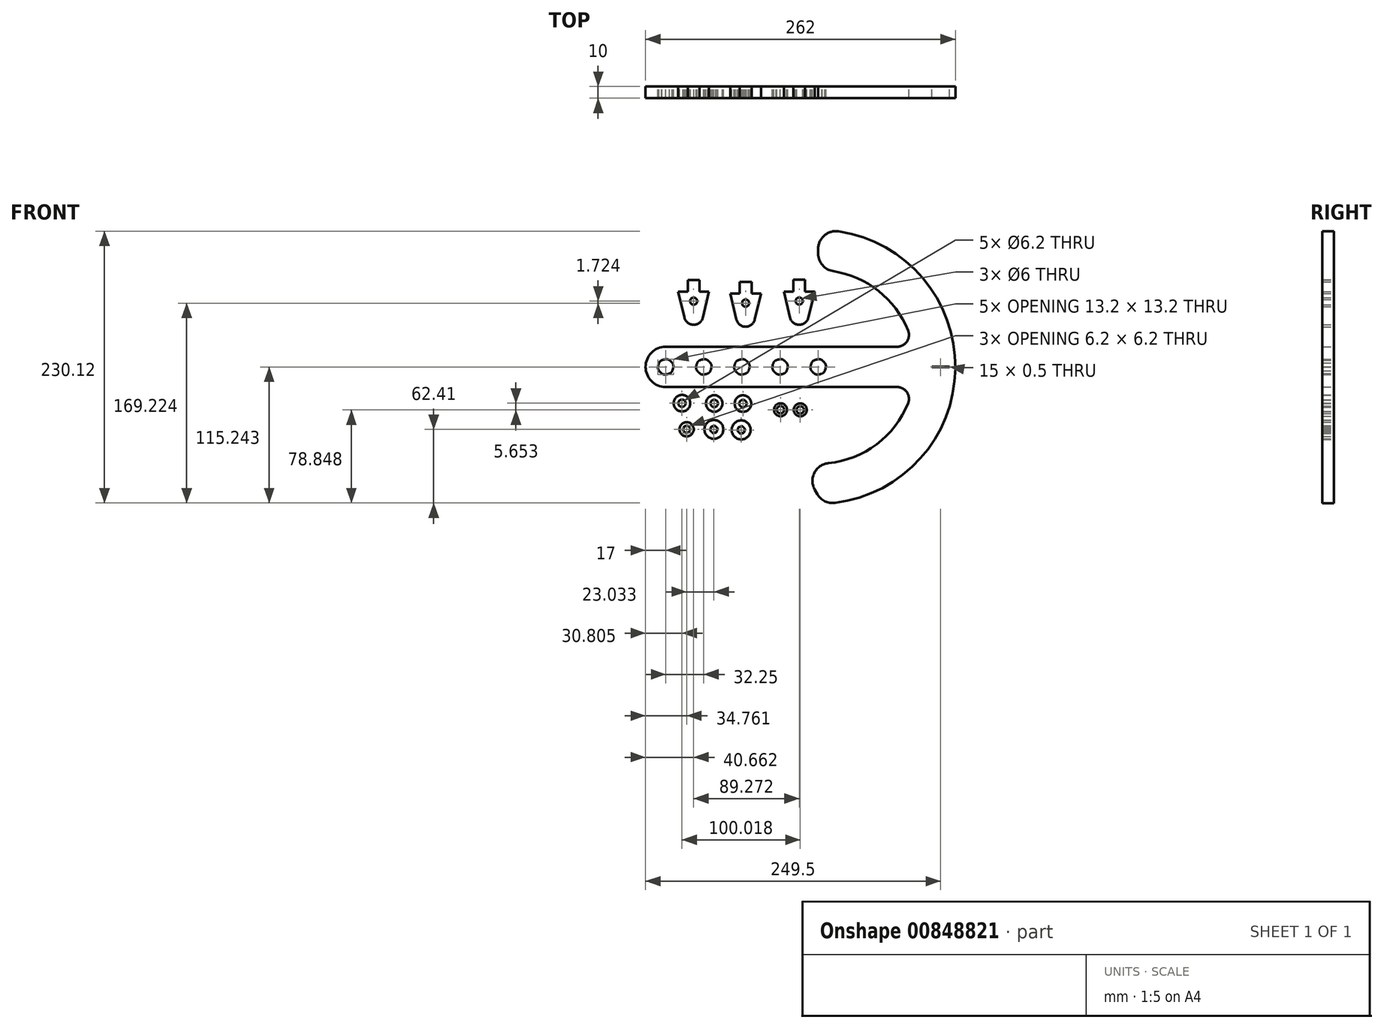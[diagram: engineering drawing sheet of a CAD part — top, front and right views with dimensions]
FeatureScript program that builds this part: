
annotation { "Feature Type Name" : "Feature", "Feature Type Description" : "" }
export const myFeature = defineFeature(function(context is Context, id is Id, definition is map)
    precondition{}
    {
        {
            var Q0;
            Q0=qCreatedBy(makeId("Front.planeOp"),FACE);
            var sketch = newSketch(context, id + "F0", { "sketchPlane" : qUnion([Q0])});
            skCircle(sketch, "E0", {"center": v(-90.34, 55.81) * mm, "radius": 3 * mm});
            skLineSegment(sketch, "E1", {"start": v(-103.34, 63.81) * mm, "end": v(-98.12, 41.96) * mm});
            skLineSegment(sketch, "E2", {"start": v(-77.34, 63.81) * mm, "end": v(-82.56, 41.96) * mm});
            skArc(sketch, "E3", {"start": v(-98.12, 41.96) * mm, "mid": v(-90.34, 35.81) * mm, "end": v(-82.56, 41.96) * mm});
            skLineSegment(sketch, "E4", {"start": v(-85.34, 63.81) * mm, "end": v(-77.34, 63.81) * mm});
            skLineSegment(sketch, "E5", {"start": v(-85.34, 73.81) * mm, "end": v(-85.34, 63.81) * mm});
            skLineSegment(sketch, "E6", {"start": v(-95.34, 73.81) * mm, "end": v(-85.34, 73.81) * mm});
            skLineSegment(sketch, "E7", {"start": v(-95.34, 63.81) * mm, "end": v(-95.34, 73.81) * mm});
            skLineSegment(sketch, "E8", {"start": v(-103.34, 63.81) * mm, "end": v(-95.34, 63.81) * mm});
            skCircle(sketch, "E9", {"center": v(-46.4, 54.16) * mm, "radius": 3 * mm});
            skLineSegment(sketch, "E10", {"start": v(-59.4, 62.16) * mm, "end": v(-54.17, 40.3) * mm});
            skLineSegment(sketch, "E11", {"start": v(-33.4, 62.16) * mm, "end": v(-38.6, 40.3) * mm});
            skArc(sketch, "E12", {"start": v(-54.17, 40.3) * mm, "mid": v(-46.4, 34.16) * mm, "end": v(-38.6, 40.3) * mm});
            skLineSegment(sketch, "E13", {"start": v(-41.4, 62.16) * mm, "end": v(-33.4, 62.16) * mm});
            skLineSegment(sketch, "E14", {"start": v(-41.4, 72.16) * mm, "end": v(-41.4, 62.16) * mm});
            skLineSegment(sketch, "E15", {"start": v(-51.4, 72.16) * mm, "end": v(-41.4, 72.16) * mm});
            skLineSegment(sketch, "E16", {"start": v(-51.4, 62.16) * mm, "end": v(-51.4, 72.16) * mm});
            skLineSegment(sketch, "E17", {"start": v(-59.4, 62.16) * mm, "end": v(-51.4, 62.16) * mm});
            skArc(sketch, "E18", {"start": v(18.3, 5.9) * mm, "mid": v(16.7, 6.56) * mm, "end": v(15, 6.78) * mm});
            skArc(sketch, "E19", {"start": v(21.6, 0.18) * mm, "mid": v(21.38, 1.9) * mm, "end": v(20.72, 3.48) * mm});
            skArc(sketch, "E20", {"start": v(18.3, -5.53) * mm, "mid": v(19.67, -4.48) * mm, "end": v(20.72, -3.12) * mm});
            skArc(sketch, "E21", {"start": v(11.7, -5.53) * mm, "mid": v(13.3, -6.2) * mm, "end": v(15, -6.42) * mm});
            skCircle(sketch, "E22", {"center": v(-1.07, 55.89) * mm, "radius": 3 * mm});
            skArc(sketch, "E23", {"start": v(8.4, 0.18) * mm, "mid": v(8.62, -1.53) * mm, "end": v(9.28, -3.12) * mm});
            skArc(sketch, "E24", {"start": v(20.54, 3.38) * mm, "mid": v(19.53, 4.7) * mm, "end": v(18.2, 5.73) * mm});
            skArc(sketch, "E25", {"start": v(20.54, -3.02) * mm, "mid": v(21.18, -1.47) * mm, "end": v(21.4, 0.18) * mm});
            skArc(sketch, "E26", {"start": v(15, -6.22) * mm, "mid": v(16.66, -6) * mm, "end": v(18.2, -5.36) * mm});
            skArc(sketch, "E27", {"start": v(9.46, -3.02) * mm, "mid": v(10.47, -4.34) * mm, "end": v(11.8, -5.36) * mm});
            skArc(sketch, "E28", {"start": v(9.46, 3.38) * mm, "mid": v(8.82, 1.84) * mm, "end": v(8.6, 0.18) * mm});
            skLineSegment(sketch, "E29", {"start": v(18.2, 5.73) * mm, "end": v(18.3, 5.9) * mm});
            skLineSegment(sketch, "E30", {"start": v(20.54, 3.38) * mm, "end": v(20.72, 3.48) * mm});
            skLineSegment(sketch, "E31", {"start": v(20.54, -3.02) * mm, "end": v(20.72, -3.12) * mm});
            skLineSegment(sketch, "E32", {"start": v(18.2, -5.36) * mm, "end": v(18.3, -5.53) * mm});
            skLineSegment(sketch, "E33", {"start": v(15, -6.22) * mm, "end": v(15, -6.42) * mm});
            skLineSegment(sketch, "E34", {"start": v(11.8, -5.36) * mm, "end": v(11.7, -5.53) * mm});
            skLineSegment(sketch, "E35", {"start": v(9.46, -3.02) * mm, "end": v(9.28, -3.12) * mm});
            skLineSegment(sketch, "E36", {"start": v(8.6, 0.18) * mm, "end": v(8.4, 0.18) * mm});
            skLineSegment(sketch, "E37", {"start": v(9.46, 3.38) * mm, "end": v(9.28, 3.48) * mm});
            skLineSegment(sketch, "E38", {"start": v(11.8, 5.73) * mm, "end": v(11.7, 5.9) * mm});
            skLineSegment(sketch, "E39", {"start": v(15, 6.58) * mm, "end": v(15, 6.78) * mm});
            skArc(sketch, "E40", {"start": v(15, 6.58) * mm, "mid": v(13.34, 6.37) * mm, "end": v(11.8, 5.73) * mm});
            skArc(sketch, "E41", {"start": v(11.7, 5.9) * mm, "mid": v(10.33, 4.85) * mm, "end": v(9.28, 3.48) * mm});
            skArc(sketch, "E42", {"start": v(-13.95, 5.9) * mm, "mid": v(-15.54, 6.56) * mm, "end": v(-17.25, 6.78) * mm});
            skArc(sketch, "E43", {"start": v(-10.65, 0.18) * mm, "mid": v(-10.87, 1.9) * mm, "end": v(-11.53, 3.48) * mm});
            skArc(sketch, "E44", {"start": v(-13.95, -5.53) * mm, "mid": v(-12.58, -4.48) * mm, "end": v(-11.53, -3.12) * mm});
            skArc(sketch, "E45", {"start": v(-20.55, -5.53) * mm, "mid": v(-18.96, -6.2) * mm, "end": v(-17.25, -6.42) * mm});
            skArc(sketch, "E46", {"start": v(-23.85, 0.18) * mm, "mid": v(-23.63, -1.53) * mm, "end": v(-22.97, -3.12) * mm});
            skArc(sketch, "E47", {"start": v(-11.7, 3.38) * mm, "mid": v(-12.72, 4.7) * mm, "end": v(-14.05, 5.73) * mm});
            skArc(sketch, "E48", {"start": v(-11.7, -3.02) * mm, "mid": v(-11.07, -1.47) * mm, "end": v(-10.85, 0.18) * mm});
            skArc(sketch, "E49", {"start": v(-17.25, -6.22) * mm, "mid": v(-15.6, -6) * mm, "end": v(-14.05, -5.36) * mm});
            skArc(sketch, "E50", {"start": v(-22.8, -3.02) * mm, "mid": v(-21.78, -4.34) * mm, "end": v(-20.45, -5.36) * mm});
            skArc(sketch, "E51", {"start": v(-22.8, 3.38) * mm, "mid": v(-23.43, 1.84) * mm, "end": v(-23.65, 0.18) * mm});
            skLineSegment(sketch, "E52", {"start": v(-14.05, 5.73) * mm, "end": v(-13.95, 5.9) * mm});
            skLineSegment(sketch, "E53", {"start": v(-119.54, 3.38) * mm, "end": v(-119.72, 3.48) * mm});
            skLineSegment(sketch, "E54", {"start": v(-117.2, 5.73) * mm, "end": v(-117.3, 5.9) * mm});
            skArc(sketch, "E55", {"start": v(-107.4, 0.18) * mm, "mid": v(-107.62, 1.9) * mm, "end": v(-108.28, 3.48) * mm});
            skArc(sketch, "E56", {"start": v(-110.7, 5.9) * mm, "mid": v(-112.3, 6.56) * mm, "end": v(-114, 6.78) * mm});
            skArc(sketch, "E57", {"start": v(-85.05, 5.9) * mm, "mid": v(-86.42, 4.85) * mm, "end": v(-87.47, 3.48) * mm});
            skArc(sketch, "E58", {"start": v(-81.75, 6.58) * mm, "mid": v(-83.4, 6.37) * mm, "end": v(-84.95, 5.73) * mm});
            skLineSegment(sketch, "E59", {"start": v(-81.75, 6.58) * mm, "end": v(-81.75, 6.78) * mm});
            skLineSegment(sketch, "E60", {"start": v(-84.95, 5.73) * mm, "end": v(-85.05, 5.9) * mm});
            skLineSegment(sketch, "E61", {"start": v(-87.3, 3.38) * mm, "end": v(-87.47, 3.48) * mm});
            skLineSegment(sketch, "E62", {"start": v(-88.15, 0.18) * mm, "end": v(-88.35, 0.18) * mm});
            skLineSegment(sketch, "E63", {"start": v(-87.3, -3.02) * mm, "end": v(-87.47, -3.12) * mm});
            skLineSegment(sketch, "E64", {"start": v(-84.95, -5.36) * mm, "end": v(-85.05, -5.53) * mm});
            skLineSegment(sketch, "E65", {"start": v(-81.75, -6.22) * mm, "end": v(-81.75, -6.42) * mm});
            skLineSegment(sketch, "E66", {"start": v(-78.55, -5.36) * mm, "end": v(-78.45, -5.53) * mm});
            skLineSegment(sketch, "E67", {"start": v(-76.2, -3.02) * mm, "end": v(-76.03, -3.12) * mm});
            skLineSegment(sketch, "E68", {"start": v(-75.35, 0.18) * mm, "end": v(-75.15, 0.18) * mm});
            skCircle(sketch, "E69", {"center": v(-0.18, -36.21) * mm, "radius": 3.1 * mm});
            skLineSegment(sketch, "E70", {"start": v(-76.2, 3.38) * mm, "end": v(-76.03, 3.48) * mm});
            skLineSegment(sketch, "E71", {"start": v(-78.55, 5.73) * mm, "end": v(-78.45, 5.9) * mm});
            skArc(sketch, "E72", {"start": v(-87.3, 3.38) * mm, "mid": v(-87.93, 1.84) * mm, "end": v(-88.15, 0.18) * mm});
            skArc(sketch, "E73", {"start": v(-81.75, -6.22) * mm, "mid": v(-80.1, -6) * mm, "end": v(-78.55, -5.36) * mm});
            skArc(sketch, "E74", {"start": v(-76.2, -3.02) * mm, "mid": v(-75.57, -1.47) * mm, "end": v(-75.35, 0.18) * mm});
            skArc(sketch, "E75", {"start": v(-76.2, 3.38) * mm, "mid": v(-77.22, 4.7) * mm, "end": v(-78.55, 5.73) * mm});
            skArc(sketch, "E76", {"start": v(-88.35, 0.18) * mm, "mid": v(-88.13, -1.53) * mm, "end": v(-87.47, -3.12) * mm});
            skArc(sketch, "E77", {"start": v(-85.05, -5.53) * mm, "mid": v(-83.46, -6.2) * mm, "end": v(-81.75, -6.42) * mm});
            skArc(sketch, "E78", {"start": v(-78.45, -5.53) * mm, "mid": v(-77.08, -4.48) * mm, "end": v(-76.03, -3.12) * mm});
            skArc(sketch, "E79", {"start": v(-75.15, 0.18) * mm, "mid": v(-75.37, 1.9) * mm, "end": v(-76.03, 3.48) * mm});
            skArc(sketch, "E80", {"start": v(-78.45, 5.9) * mm, "mid": v(-80.04, 6.56) * mm, "end": v(-81.75, 6.78) * mm});
            skArc(sketch, "E81", {"start": v(-52.8, 5.9) * mm, "mid": v(-54.17, 4.85) * mm, "end": v(-55.22, 3.48) * mm});
            skLineSegment(sketch, "E82", {"start": v(-49.5, 6.58) * mm, "end": v(-49.5, 6.78) * mm});
            skLineSegment(sketch, "E83", {"start": v(-52.7, 5.73) * mm, "end": v(-52.8, 5.9) * mm});
            skLineSegment(sketch, "E84", {"start": v(-55.04, 3.38) * mm, "end": v(-55.22, 3.48) * mm});
            skLineSegment(sketch, "E85", {"start": v(-55.9, 0.18) * mm, "end": v(-56.1, 0.18) * mm});
            skLineSegment(sketch, "E86", {"start": v(-55.04, -3.02) * mm, "end": v(-55.22, -3.12) * mm});
            skLineSegment(sketch, "E87", {"start": v(-52.7, -5.36) * mm, "end": v(-52.8, -5.53) * mm});
            skLineSegment(sketch, "E88", {"start": v(-49.5, -6.22) * mm, "end": v(-49.5, -6.42) * mm});
            skLineSegment(sketch, "E89", {"start": v(-46.3, -5.36) * mm, "end": v(-46.2, -5.53) * mm});
            skLineSegment(sketch, "E90", {"start": v(-43.96, -3.02) * mm, "end": v(-43.78, -3.12) * mm});
            skLineSegment(sketch, "E91", {"start": v(-43.1, 0.18) * mm, "end": v(-42.9, 0.18) * mm});
            skLineSegment(sketch, "E92", {"start": v(-43.96, 3.38) * mm, "end": v(-43.78, 3.48) * mm});
            skLineSegment(sketch, "E93", {"start": v(-46.3, 5.73) * mm, "end": v(-46.2, 5.9) * mm});
            skArc(sketch, "E94", {"start": v(-55.04, 3.38) * mm, "mid": v(-55.68, 1.84) * mm, "end": v(-55.9, 0.18) * mm});
            skLineSegment(sketch, "E95", {"start": v(-6.07, 73.89) * mm, "end": v(3.93, 73.89) * mm});
            skLineSegment(sketch, "E96", {"start": v(3.93, 73.89) * mm, "end": v(3.93, 63.89) * mm});
            skArc(sketch, "E97", {"start": v(-8.85, 42.03) * mm, "mid": v(-1.07, 35.89) * mm, "end": v(6.72, 42.03) * mm});
            skCircle(sketch, "E98", {"center": v(-96.24, -52.65) * mm, "radius": 6 * mm});
            skLineSegment(sketch, "E99", {"start": v(11.93, 63.89) * mm, "end": v(6.72, 42.03) * mm});
            skLineSegment(sketch, "E100", {"start": v(-14.07, 63.89) * mm, "end": v(-8.85, 42.03) * mm});
            skArc(sketch, "E101", {"start": v(-114, 17.18) * mm, "mid": v(-131, 0.18) * mm, "end": v(-114, -16.82) * mm});
            skLineSegment(sketch, "E102", {"start": v(-114, -16.82) * mm, "end": v(81.75, -16.82) * mm});
            skLineSegment(sketch, "E103", {"start": v(-114, 17.18) * mm, "end": v(81.75, 17.18) * mm});
            skArc(sketch, "E104", {"start": v(29.15, -114.95) * mm, "mid": v(130.99, -1.37) * mm, "end": v(32.23, 114.9) * mm});
            skLineSegment(sketch, "E105", {"start": v(15, 96.02) * mm, "end": v(15, 100.06) * mm});
            skLineSegment(sketch, "E106", {"start": v(12.16, -103.88) * mm, "end": v(14.38, -107.65) * mm});
            skCircle(sketch, "E107", {"center": v(-100.2, -30.56) * mm, "radius": 3.1 * mm});
            skArc(sketch, "E108", {"start": v(-120.6, 0.18) * mm, "mid": v(-120.38, -1.53) * mm, "end": v(-119.72, -3.12) * mm});
            skArc(sketch, "E109", {"start": v(81.75, 17.18) * mm, "mid": v(90.04, 21.6) * mm, "end": v(91.02, 30.93) * mm});
            skArc(sketch, "E110", {"start": v(-55.04, -3.02) * mm, "mid": v(-54.03, -4.34) * mm, "end": v(-52.7, -5.36) * mm});
            skCircle(sketch, "E111", {"center": v(-72.95, -30.75) * mm, "radius": 3.1 * mm});
            skArc(sketch, "E112", {"start": v(-117.3, -5.53) * mm, "mid": v(-115.7, -6.2) * mm, "end": v(-114, -6.42) * mm});
            skArc(sketch, "E113", {"start": v(91.02, -30.57) * mm, "mid": v(90.04, -21.23) * mm, "end": v(81.75, -16.82) * mm});
            skArc(sketch, "E114", {"start": v(-49.5, -6.22) * mm, "mid": v(-47.84, -6) * mm, "end": v(-46.3, -5.36) * mm});
            skLineSegment(sketch, "E115", {"start": v(3.93, 63.89) * mm, "end": v(11.93, 63.89) * mm});
            skArc(sketch, "E116", {"start": v(-87.3, -3.02) * mm, "mid": v(-86.28, -4.34) * mm, "end": v(-84.95, -5.36) * mm});
            skCircle(sketch, "E117", {"center": v(-73.2, -52.76) * mm, "radius": 8 * mm});
            skLineSegment(sketch, "E118", {"start": v(-71.76, -50.25) * mm, "end": v(-71.66, -50.07) * mm});
            skLineSegment(sketch, "E119", {"start": v(-110.8, 5.73) * mm, "end": v(-110.7, 5.9) * mm});
            skArc(sketch, "E120", {"start": v(23.54, -81.37) * mm, "mid": v(64.32, -65.32) * mm, "end": v(91.02, -30.57) * mm});
            skArc(sketch, "E121", {"start": v(-110.7, -5.53) * mm, "mid": v(-109.33, -4.48) * mm, "end": v(-108.28, -3.12) * mm});
            skArc(sketch, "E122", {"start": v(-74.76, -50.07) * mm, "mid": v(-75.4, -50.57) * mm, "end": v(-75.9, -51.2) * mm});
            skArc(sketch, "E123", {"start": v(-43.96, -3.02) * mm, "mid": v(-43.32, -1.47) * mm, "end": v(-43.1, 0.18) * mm});
            skCircle(sketch, "E124", {"center": v(-0.18, -36.21) * mm, "radius": 5.5 * mm});
            skArc(sketch, "E125", {"start": v(-108.46, 3.38) * mm, "mid": v(-109.47, 4.7) * mm, "end": v(-110.8, 5.73) * mm});
            skArc(sketch, "E126", {"start": v(32.23, 114.9) * mm, "mid": v(20.21, 111.43) * mm, "end": v(15, 100.06) * mm});
            skArc(sketch, "E127", {"start": v(-108.46, -3.02) * mm, "mid": v(-107.82, -1.47) * mm, "end": v(-107.6, 0.18) * mm});
            skArc(sketch, "E128", {"start": v(15, 96.02) * mm, "mid": v(18.6, 86.26) * mm, "end": v(27.68, 81.2) * mm});
            skArc(sketch, "E129", {"start": v(-114, -6.22) * mm, "mid": v(-112.34, -6) * mm, "end": v(-110.8, -5.36) * mm});
            skLineSegment(sketch, "E130", {"start": v(21.4, 0.18) * mm, "end": v(21.6, 0.18) * mm});
            skCircle(sketch, "E131", {"center": v(-16.86, -36.1) * mm, "radius": 3.1 * mm});
            skArc(sketch, "E132", {"start": v(23.54, -81.37) * mm, "mid": v(11.72, -89.52) * mm, "end": v(12.16, -103.88) * mm});
            skArc(sketch, "E133", {"start": v(-119.54, -3.02) * mm, "mid": v(-118.53, -4.34) * mm, "end": v(-117.2, -5.36) * mm});
            skArc(sketch, "E134", {"start": v(14.38, -107.65) * mm, "mid": v(20.67, -113.5) * mm, "end": v(29.15, -114.95) * mm});
            skArc(sketch, "E135", {"start": v(-119.54, 3.38) * mm, "mid": v(-120.18, 1.84) * mm, "end": v(-120.4, 0.18) * mm});
            skLineSegment(sketch, "E136", {"start": v(-6.07, 63.89) * mm, "end": v(-6.07, 73.89) * mm});
            skLineSegment(sketch, "E137", {"start": v(-14.07, 63.89) * mm, "end": v(-6.07, 63.89) * mm});
            skLineSegment(sketch, "E138", {"start": v(-11.7, 3.38) * mm, "end": v(-11.53, 3.48) * mm});
            skLineSegment(sketch, "E139", {"start": v(-10.85, 0.18) * mm, "end": v(-10.65, 0.18) * mm});
            skLineSegment(sketch, "E140", {"start": v(-11.7, -3.02) * mm, "end": v(-11.53, -3.12) * mm});
            skLineSegment(sketch, "E141", {"start": v(-14.05, -5.36) * mm, "end": v(-13.95, -5.53) * mm});
            skLineSegment(sketch, "E142", {"start": v(-17.25, -6.22) * mm, "end": v(-17.25, -6.42) * mm});
            skLineSegment(sketch, "E143", {"start": v(-20.45, -5.36) * mm, "end": v(-20.55, -5.53) * mm});
            skLineSegment(sketch, "E144", {"start": v(-23.65, 0.18) * mm, "end": v(-23.85, 0.18) * mm});
            skLineSegment(sketch, "E145", {"start": v(-22.8, 3.38) * mm, "end": v(-22.97, 3.48) * mm});
            skArc(sketch, "E146", {"start": v(91.02, 30.93) * mm, "mid": v(65.97, 64.41) * mm, "end": v(27.68, 81.2) * mm});
            skCircle(sketch, "E147", {"center": v(-50.1, -53.16) * mm, "radius": 8 * mm});
            skLineSegment(sketch, "E148", {"start": v(-20.45, 5.73) * mm, "end": v(-20.55, 5.9) * mm});
            skLineSegment(sketch, "E149", {"start": v(-17.25, 6.58) * mm, "end": v(-17.25, 6.78) * mm});
            skArc(sketch, "E150", {"start": v(-17.25, 6.58) * mm, "mid": v(-18.9, 6.37) * mm, "end": v(-20.45, 5.73) * mm});
            skArc(sketch, "E151", {"start": v(-20.55, 5.9) * mm, "mid": v(-21.92, 4.85) * mm, "end": v(-22.97, 3.48) * mm});
            skArc(sketch, "E152", {"start": v(-46.2, 5.9) * mm, "mid": v(-47.8, 6.56) * mm, "end": v(-49.5, 6.78) * mm});
            skArc(sketch, "E153", {"start": v(-42.9, 0.18) * mm, "mid": v(-43.12, 1.9) * mm, "end": v(-43.78, 3.48) * mm});
            skArc(sketch, "E154", {"start": v(-46.2, -5.53) * mm, "mid": v(-44.83, -4.48) * mm, "end": v(-43.78, -3.12) * mm});
            skArc(sketch, "E155", {"start": v(-52.8, -5.53) * mm, "mid": v(-51.2, -6.2) * mm, "end": v(-49.5, -6.42) * mm});
            skArc(sketch, "E156", {"start": v(-56.1, 0.18) * mm, "mid": v(-55.88, -1.53) * mm, "end": v(-55.22, -3.12) * mm});
            skArc(sketch, "E157", {"start": v(-43.96, 3.38) * mm, "mid": v(-44.97, 4.7) * mm, "end": v(-46.3, 5.73) * mm});
            skCircle(sketch, "E158", {"center": v(-16.86, -36.1) * mm, "radius": 5.5 * mm});
            skLineSegment(sketch, "E159", {"start": v(-108.46, 3.38) * mm, "end": v(-108.28, 3.48) * mm});
            skLineSegment(sketch, "E160", {"start": v(-107.6, 0.18) * mm, "end": v(-107.4, 0.18) * mm});
            skLineSegment(sketch, "E161", {"start": v(-108.46, -3.02) * mm, "end": v(-108.28, -3.12) * mm});
            skLineSegment(sketch, "E162", {"start": v(-110.8, -5.36) * mm, "end": v(-110.7, -5.53) * mm});
            skLineSegment(sketch, "E163", {"start": v(-114, -6.22) * mm, "end": v(-114, -6.42) * mm});
            skLineSegment(sketch, "E164", {"start": v(-117.2, -5.36) * mm, "end": v(-117.3, -5.53) * mm});
            skLineSegment(sketch, "E165", {"start": v(-119.54, -3.02) * mm, "end": v(-119.72, -3.12) * mm});
            skLineSegment(sketch, "E166", {"start": v(-120.4, 0.18) * mm, "end": v(-120.6, 0.18) * mm});
            skArc(sketch, "E167", {"start": v(-94.69, -55.34) * mm, "mid": v(-94.05, -54.84) * mm, "end": v(-93.55, -54.2) * mm});
            skArc(sketch, "E168", {"start": v(-97.79, -55.34) * mm, "mid": v(-97.04, -55.64) * mm, "end": v(-96.24, -55.75) * mm});
            skArc(sketch, "E169", {"start": v(-99.34, -52.65) * mm, "mid": v(-99.23, -53.45) * mm, "end": v(-98.92, -54.2) * mm});
            skArc(sketch, "E170", {"start": v(-93.73, -51.2) * mm, "mid": v(-94.19, -50.6) * mm, "end": v(-94.79, -50.14) * mm});
            skArc(sketch, "E171", {"start": v(-93.73, -54.1) * mm, "mid": v(-93.44, -53.4) * mm, "end": v(-93.34, -52.65) * mm});
            skArc(sketch, "E172", {"start": v(-96.24, -55.55) * mm, "mid": v(-95.49, -55.45) * mm, "end": v(-94.79, -55.16) * mm});
            skArc(sketch, "E173", {"start": v(-98.75, -54.1) * mm, "mid": v(-98.29, -54.7) * mm, "end": v(-97.69, -55.16) * mm});
            skArc(sketch, "E174", {"start": v(-98.75, -51.2) * mm, "mid": v(-99.04, -51.9) * mm, "end": v(-99.14, -52.65) * mm});
            skLineSegment(sketch, "E175", {"start": v(-94.79, -50.14) * mm, "end": v(-94.69, -49.97) * mm});
            skLineSegment(sketch, "E176", {"start": v(-93.73, -51.2) * mm, "end": v(-93.55, -51.1) * mm});
            skLineSegment(sketch, "E177", {"start": v(-93.34, -52.65) * mm, "end": v(-93.14, -52.65) * mm});
            skLineSegment(sketch, "E178", {"start": v(-93.73, -54.1) * mm, "end": v(-93.55, -54.2) * mm});
            skLineSegment(sketch, "E179", {"start": v(-94.79, -55.16) * mm, "end": v(-94.69, -55.34) * mm});
            skLineSegment(sketch, "E180", {"start": v(-96.24, -55.55) * mm, "end": v(-96.24, -55.75) * mm});
            skCircle(sketch, "E181", {"center": v(-48.63, -30.86) * mm, "radius": 3.1 * mm});
            skLineSegment(sketch, "E182", {"start": v(-97.69, -55.16) * mm, "end": v(-97.79, -55.34) * mm});
            skLineSegment(sketch, "E183", {"start": v(-98.75, -54.1) * mm, "end": v(-98.92, -54.2) * mm});
            skLineSegment(sketch, "E184", {"start": v(-99.14, -52.65) * mm, "end": v(-99.34, -52.65) * mm});
            skLineSegment(sketch, "E185", {"start": v(-98.75, -51.2) * mm, "end": v(-98.92, -51.1) * mm});
            skLineSegment(sketch, "E186", {"start": v(-97.69, -50.14) * mm, "end": v(-97.79, -49.97) * mm});
            skLineSegment(sketch, "E187", {"start": v(-96.24, -49.75) * mm, "end": v(-96.24, -49.55) * mm});
            skArc(sketch, "E188", {"start": v(-96.24, -49.75) * mm, "mid": v(-96.99, -49.85) * mm, "end": v(-97.69, -50.14) * mm});
            skArc(sketch, "E189", {"start": v(-97.79, -49.97) * mm, "mid": v(-98.43, -50.46) * mm, "end": v(-98.92, -51.1) * mm});
            skArc(sketch, "E190", {"start": v(-71.66, -50.07) * mm, "mid": v(-72.4, -49.76) * mm, "end": v(-73.2, -49.66) * mm});
            skLineSegment(sketch, "E191", {"start": v(-70.7, -54.2) * mm, "end": v(-70.52, -54.3) * mm});
            skLineSegment(sketch, "E192", {"start": v(-71.76, -55.27) * mm, "end": v(-71.66, -55.44) * mm});
            skLineSegment(sketch, "E193", {"start": v(-73.2, -55.66) * mm, "end": v(-73.2, -55.86) * mm});
            skLineSegment(sketch, "E194", {"start": v(-74.66, -55.27) * mm, "end": v(-74.76, -55.44) * mm});
            skLineSegment(sketch, "E195", {"start": v(-75.72, -54.2) * mm, "end": v(-75.9, -54.3) * mm});
            skLineSegment(sketch, "E196", {"start": v(-76.1, -52.76) * mm, "end": v(-76.3, -52.76) * mm});
            skCircle(sketch, "E197", {"center": v(-72.95, -30.75) * mm, "radius": 7 * mm});
            skArc(sketch, "E198", {"start": v(-73.2, -49.86) * mm, "mid": v(-73.96, -49.96) * mm, "end": v(-74.66, -50.25) * mm});
            skLineSegment(sketch, "E199", {"start": v(-73.2, -49.86) * mm, "end": v(-73.2, -49.66) * mm});
            skLineSegment(sketch, "E200", {"start": v(-74.66, -50.25) * mm, "end": v(-74.76, -50.07) * mm});
            skLineSegment(sketch, "E201", {"start": v(-75.72, -51.3) * mm, "end": v(-75.9, -51.2) * mm});
            skLineSegment(sketch, "E202", {"start": v(-70.3, -52.76) * mm, "end": v(-70.1, -52.76) * mm});
            skLineSegment(sketch, "E203", {"start": v(-70.7, -51.3) * mm, "end": v(-70.52, -51.2) * mm});
            skArc(sketch, "E204", {"start": v(-75.72, -51.3) * mm, "mid": v(-76, -52) * mm, "end": v(-76.1, -52.76) * mm});
            skArc(sketch, "E205", {"start": v(-75.72, -54.2) * mm, "mid": v(-75.26, -54.8) * mm, "end": v(-74.66, -55.27) * mm});
            skArc(sketch, "E206", {"start": v(-73.2, -55.66) * mm, "mid": v(-72.46, -55.56) * mm, "end": v(-71.76, -55.27) * mm});
            skArc(sketch, "E207", {"start": v(-70.7, -54.2) * mm, "mid": v(-70.4, -53.5) * mm, "end": v(-70.3, -52.76) * mm});
            skArc(sketch, "E208", {"start": v(-70.7, -51.3) * mm, "mid": v(-71.16, -50.7) * mm, "end": v(-71.76, -50.25) * mm});
            skArc(sketch, "E209", {"start": v(-76.3, -52.76) * mm, "mid": v(-76.2, -53.56) * mm, "end": v(-75.9, -54.3) * mm});
            skArc(sketch, "E210", {"start": v(-74.76, -55.44) * mm, "mid": v(-74, -55.75) * mm, "end": v(-73.2, -55.86) * mm});
            skArc(sketch, "E211", {"start": v(-71.66, -55.44) * mm, "mid": v(-71.01, -54.95) * mm, "end": v(-70.52, -54.3) * mm});
            skCircle(sketch, "E212", {"center": v(-100.2, -30.56) * mm, "radius": 7 * mm});
            skArc(sketch, "E213", {"start": v(-70.1, -52.76) * mm, "mid": v(-70.21, -51.96) * mm, "end": v(-70.52, -51.2) * mm});
            skArc(sketch, "E214", {"start": v(-93.14, -52.65) * mm, "mid": v(-93.24, -51.85) * mm, "end": v(-93.55, -51.1) * mm});
            skArc(sketch, "E215", {"start": v(-94.69, -49.97) * mm, "mid": v(-95.44, -49.66) * mm, "end": v(-96.24, -49.55) * mm});
            skArc(sketch, "E216", {"start": v(-51.65, -50.48) * mm, "mid": v(-52.3, -50.97) * mm, "end": v(-52.79, -51.61) * mm});
            skArc(sketch, "E217", {"start": v(-50.1, -50.26) * mm, "mid": v(-50.85, -50.36) * mm, "end": v(-51.55, -50.65) * mm});
            skLineSegment(sketch, "E218", {"start": v(-50.1, -50.26) * mm, "end": v(-50.1, -50.06) * mm});
            skLineSegment(sketch, "E219", {"start": v(-51.55, -50.65) * mm, "end": v(-51.65, -50.48) * mm});
            skArc(sketch, "E220", {"start": v(-49.5, 6.58) * mm, "mid": v(-51.16, 6.37) * mm, "end": v(-52.7, 5.73) * mm});
            skLineSegment(sketch, "E221", {"start": v(-52.61, -51.71) * mm, "end": v(-52.79, -51.61) * mm});
            skLineSegment(sketch, "E222", {"start": v(-53, -53.16) * mm, "end": v(-53.2, -53.16) * mm});
            skLineSegment(sketch, "E223", {"start": v(-52.61, -54.61) * mm, "end": v(-52.79, -54.71) * mm});
            skLineSegment(sketch, "E224", {"start": v(-51.55, -55.67) * mm, "end": v(-51.65, -55.85) * mm});
            skLineSegment(sketch, "E225", {"start": v(-50.1, -56.06) * mm, "end": v(-50.1, -56.26) * mm});
            skLineSegment(sketch, "E226", {"start": v(-48.65, -55.67) * mm, "end": v(-48.55, -55.85) * mm});
            skLineSegment(sketch, "E227", {"start": v(-47.59, -54.61) * mm, "end": v(-47.42, -54.71) * mm});
            skLineSegment(sketch, "E228", {"start": v(-47.2, -53.16) * mm, "end": v(-47, -53.16) * mm});
            skLineSegment(sketch, "E229", {"start": v(-47.59, -51.71) * mm, "end": v(-47.42, -51.61) * mm});
            skLineSegment(sketch, "E230", {"start": v(-48.65, -50.65) * mm, "end": v(-48.55, -50.48) * mm});
            skArc(sketch, "E231", {"start": v(-52.61, -51.71) * mm, "mid": v(-52.9, -52.41) * mm, "end": v(-53, -53.16) * mm});
            skCircle(sketch, "E232", {"center": v(-48.63, -30.86) * mm, "radius": 7 * mm});
            skArc(sketch, "E233", {"start": v(-52.61, -54.61) * mm, "mid": v(-52.15, -55.21) * mm, "end": v(-51.55, -55.67) * mm});
            skArc(sketch, "E234", {"start": v(-50.1, -56.06) * mm, "mid": v(-49.35, -55.96) * mm, "end": v(-48.65, -55.67) * mm});
            skArc(sketch, "E235", {"start": v(-47.59, -54.61) * mm, "mid": v(-47.3, -53.91) * mm, "end": v(-47.2, -53.16) * mm});
            skArc(sketch, "E236", {"start": v(-47.59, -51.71) * mm, "mid": v(-48.05, -51.11) * mm, "end": v(-48.65, -50.65) * mm});
            skArc(sketch, "E237", {"start": v(-53.2, -53.16) * mm, "mid": v(-53.1, -53.97) * mm, "end": v(-52.79, -54.71) * mm});
            skArc(sketch, "E238", {"start": v(-51.65, -55.85) * mm, "mid": v(-50.9, -56.16) * mm, "end": v(-50.1, -56.26) * mm});
            skArc(sketch, "E239", {"start": v(-48.55, -55.85) * mm, "mid": v(-47.9, -55.36) * mm, "end": v(-47.42, -54.71) * mm});
            skArc(sketch, "E240", {"start": v(-47, -53.16) * mm, "mid": v(-47.1, -52.36) * mm, "end": v(-47.42, -51.61) * mm});
            skArc(sketch, "E241", {"start": v(-48.55, -50.48) * mm, "mid": v(-49.3, -50.17) * mm, "end": v(-50.1, -50.06) * mm});
            skLineSegment(sketch, "E242", {"start": v(-22.8, -3.02) * mm, "end": v(-22.97, -3.12) * mm});
            skLineSegment(sketch, "E243", {"start": v(111, 0.43) * mm, "end": v(126, 0.43) * mm});
            skLineSegment(sketch, "E244", {"start": v(126, 0.43) * mm, "end": v(126, -0.07) * mm});
            skLineSegment(sketch, "E245", {"start": v(126, -0.07) * mm, "end": v(111, -0.07) * mm});
            skLineSegment(sketch, "E246", {"start": v(111, 0.43) * mm, "end": v(111, -0.07) * mm});
            skArc(sketch, "E247", {"start": v(-117.3, 5.9) * mm, "mid": v(-118.67, 4.85) * mm, "end": v(-119.72, 3.48) * mm});
            skArc(sketch, "E248", {"start": v(-114, 6.58) * mm, "mid": v(-115.66, 6.37) * mm, "end": v(-117.2, 5.73) * mm});
            skLineSegment(sketch, "E249", {"start": v(-114, 6.58) * mm, "end": v(-114, 6.78) * mm});
            skSolve(sketch);
        }
        {
            var Q0;
            Q0 = qSketchRegion(id + "F0", true);
            extrude(context, id + "F1", {"entities" : qUnion([Q0]), "depth" : 10 * mm, "offsetDistance" : 25 * mm});
        }
    });
